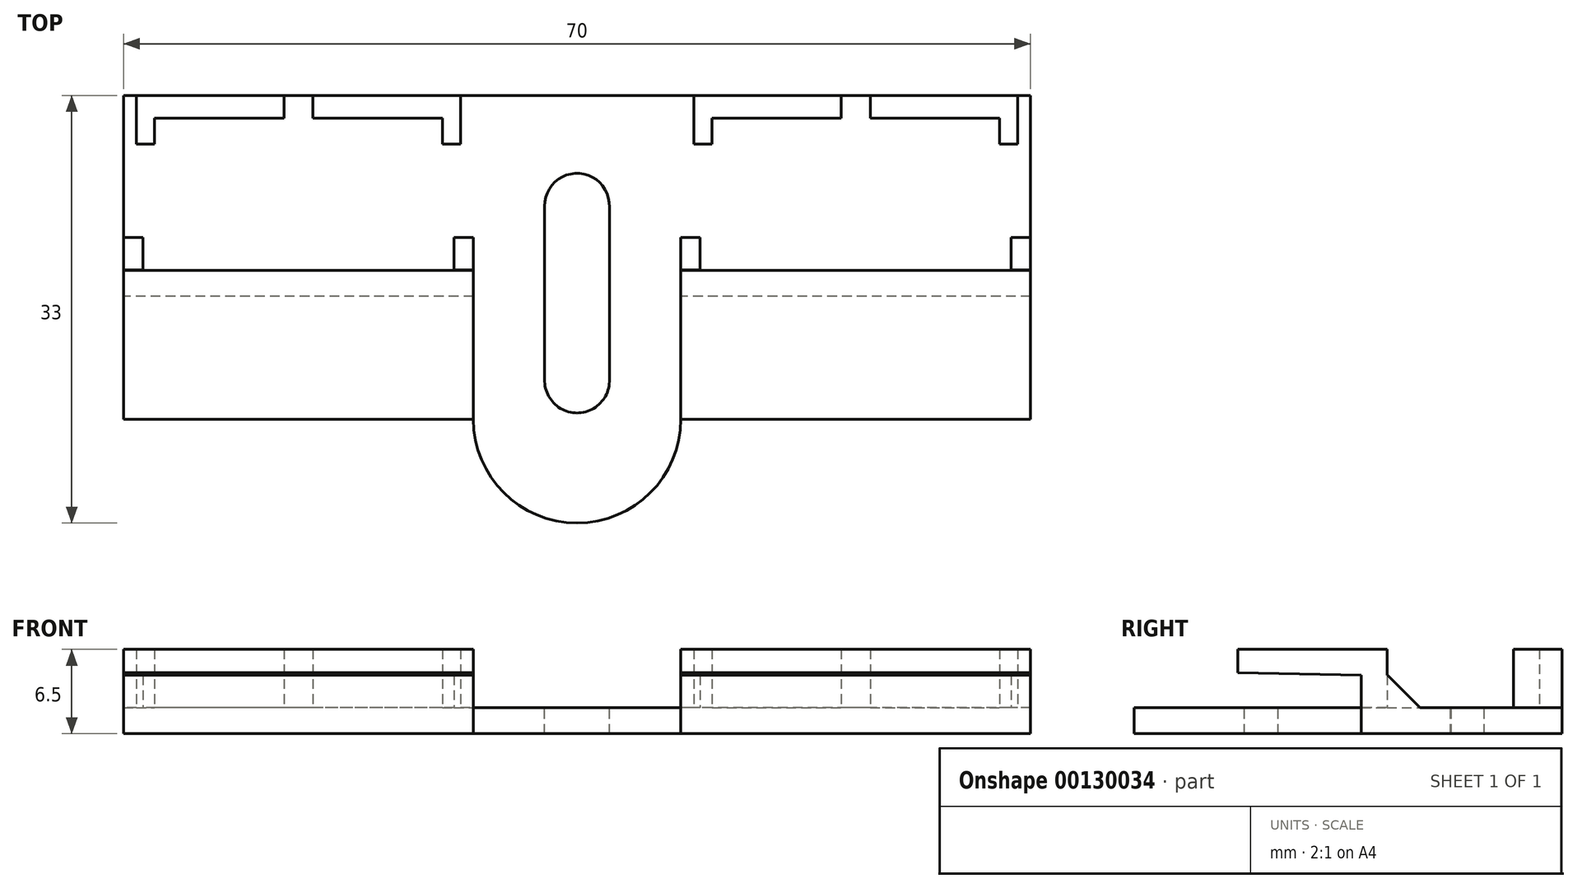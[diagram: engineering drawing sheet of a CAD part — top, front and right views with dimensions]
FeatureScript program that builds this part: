
annotation { "Feature Type Name" : "Feature", "Feature Type Description" : "" }
export const myFeature = defineFeature(function(context is Context, id is Id, definition is map)
    precondition{}
    {
        {
            var Q0;
            Q0=qCreatedBy(makeId("Right.planeOp"),FACE);
            var sketch = newSketch(context, id + "F0", { "sketchPlane" : qUnion([Q0])});
            skLineSegment(sketch, "E0.top", {"start": v(0, 2) * mm, "end": v(-13.5, 2) * mm});
            skLineSegment(sketch, "E0.left", {"start": v(0, 0) * mm, "end": v(0, 2) * mm});
            skLineSegment(sketch, "E1.right", {"start": v(-25, 6.5) * mm, "end": v(-25, 4.7) * mm});
            skLineSegment(sketch, "E2", {"start": v(-25, 4.7) * mm, "end": v(-15.5, 4.5) * mm});
            skLineSegment(sketch, "E3", {"start": v(-13.5, 6.5) * mm, "end": v(-13.5, 2) * mm});
            skLineSegment(sketch, "E4", {"start": v(-25, 6.5) * mm, "end": v(-13.5, 6.5) * mm});
            skLineSegment(sketch, "E5", {"start": v(-15.5, 4.5) * mm, "end": v(-15.5, 0) * mm});
            skLineSegment(sketch, "E6", {"start": v(-15.5, 0) * mm, "end": v(0, 0) * mm});
            skSolve(sketch);
        }
        {
            var Q0;
            Q0=makeQuery(id+"F0.imprint","IMPRINT",FACE,{"disambiguationData":[TD([[makeQuery(id+"F0.imprint","IMPRINT",EDGE,{"derivedFrom":sQuery(id+"F0.wireOp",EDGE,"E0.top")}),1.0]])]});
            extrude(context, id + "F1", {"entities" : qUnion([Q0]), "depth" : 35 * mm, "hasSecondDirection" : true, "secondDirectionOppositeDirection" : true, "secondDirectionDepth" : 35 * mm});
        }
        {
            var Q0;
            Q0=qCreatedBy(makeId("Top.planeOp"),FACE);
            var sketch = newSketch(context, id + "F2", { "sketchPlane" : qUnion([Q0])});
            skLineSegment(sketch, "E7.bottom", {"start": v(-34, 0) * mm, "end": v(-22.63, 0) * mm});
            skLineSegment(sketch, "E7.top", {"start": v(-34, -3.75) * mm, "end": v(-32.6, -3.75) * mm});
            skLineSegment(sketch, "E7.left", {"start": v(-34, 0) * mm, "end": v(-34, -3.75) * mm});
            skLineSegment(sketch, "E7.right", {"start": v(-9, 0) * mm, "end": v(-9, -3.75) * mm});
            skLineSegment(sketch, "E8.top", {"start": v(-10.4, -1.75) * mm, "end": v(-20.38, -1.75) * mm});
            skLineSegment(sketch, "E8.left", {"start": v(-10.4, -3.75) * mm, "end": v(-10.4, -1.75) * mm});
            skLineSegment(sketch, "E8.right", {"start": v(-32.6, -3.75) * mm, "end": v(-32.6, -1.75) * mm});
            skLineSegment(sketch, "E9.trimOffspring", {"start": v(-10.4, -3.75) * mm, "end": v(-9, -3.75) * mm});
            skLineSegment(sketch, "E10.left", {"start": v(-20.38, -1.75) * mm, "end": v(-20.38, 0) * mm});
            skLineSegment(sketch, "E10.right", {"start": v(-22.63, -1.75) * mm, "end": v(-22.63, 0) * mm});
            skLineSegment(sketch, "E11.trimOffspring", {"start": v(-20.38, 0) * mm, "end": v(-9, 0) * mm});
            skLineSegment(sketch, "E12.trimOffspring", {"start": v(-22.63, -1.75) * mm, "end": v(-32.6, -1.75) * mm});
            skLineSegment(sketch, "E13.MirrorCS", {"start": v(9, 0) * mm, "end": v(9, -3.75) * mm});
            skLineSegment(sketch, "E14.MirrorCS", {"start": v(10.4, -3.75) * mm, "end": v(9, -3.75) * mm});
            skLineSegment(sketch, "E15.MirrorCS", {"start": v(10.4, -1.75) * mm, "end": v(20.38, -1.75) * mm});
            skLineSegment(sketch, "E16.MirrorCS", {"start": v(20.38, 0) * mm, "end": v(9, 0) * mm});
            skLineSegment(sketch, "E17.MirrorCS", {"start": v(20.38, -1.75) * mm, "end": v(20.38, 0) * mm});
            skLineSegment(sketch, "E18.MirrorCS", {"start": v(22.63, -1.75) * mm, "end": v(22.63, 0) * mm});
            skLineSegment(sketch, "E19.MirrorCS", {"start": v(22.63, -1.75) * mm, "end": v(32.6, -1.75) * mm});
            skLineSegment(sketch, "E20.MirrorCS", {"start": v(34, 0) * mm, "end": v(22.63, 0) * mm});
            skLineSegment(sketch, "E21.MirrorCS", {"start": v(34, 0) * mm, "end": v(34, -3.75) * mm});
            skLineSegment(sketch, "E22.MirrorCS", {"start": v(34, -3.75) * mm, "end": v(32.6, -3.75) * mm});
            skLineSegment(sketch, "E23.MirrorCS", {"start": v(32.6, -3.75) * mm, "end": v(32.6, -1.75) * mm});
            skLineSegment(sketch, "E24.MirrorCS", {"start": v(10.4, -3.75) * mm, "end": v(10.4, -1.75) * mm});
            skLineSegment(sketch, "E25.bottom", {"start": v(-35, -13.5) * mm, "end": v(-33.5, -13.5) * mm});
            skLineSegment(sketch, "E25.top", {"start": v(-33.5, -10.25) * mm, "end": v(-35, -10.25) * mm});
            skLineSegment(sketch, "E25.left", {"start": v(-33.5, -13.5) * mm, "end": v(-33.5, -10.25) * mm});
            skLineSegment(sketch, "E25.right", {"start": v(-35, -13.5) * mm, "end": v(-35, -10.25) * mm});
            skLineSegment(sketch, "E26.bottom", {"start": v(-8, -13.5) * mm, "end": v(-9.5, -13.5) * mm});
            skLineSegment(sketch, "E26.top", {"start": v(-8, -10.25) * mm, "end": v(-9.5, -10.25) * mm});
            skLineSegment(sketch, "E26.left", {"start": v(-8, -13.5) * mm, "end": v(-8, -10.25) * mm});
            skLineSegment(sketch, "E26.right", {"start": v(-9.5, -13.5) * mm, "end": v(-9.5, -10.25) * mm});
            skLineSegment(sketch, "E27.MirrorCS", {"start": v(8, -13.5) * mm, "end": v(8, -10.25) * mm});
            skLineSegment(sketch, "E28.MirrorCS", {"start": v(8, -13.5) * mm, "end": v(9.5, -13.5) * mm});
            skLineSegment(sketch, "E29.MirrorCS", {"start": v(8, -10.25) * mm, "end": v(9.5, -10.25) * mm});
            skLineSegment(sketch, "E30.MirrorCS", {"start": v(9.5, -13.5) * mm, "end": v(9.5, -10.25) * mm});
            skLineSegment(sketch, "E31.MirrorCS", {"start": v(33.5, -13.5) * mm, "end": v(33.5, -10.25) * mm});
            skLineSegment(sketch, "E32.MirrorCS", {"start": v(35, -13.5) * mm, "end": v(35, -10.25) * mm});
            skLineSegment(sketch, "E33.MirrorCS", {"start": v(33.5, -10.25) * mm, "end": v(35, -10.25) * mm});
            skLineSegment(sketch, "E34.MirrorCS", {"start": v(35, -13.5) * mm, "end": v(33.5, -13.5) * mm});
            skPoint(sketch, "E35", {"position": v(21.5, -7.63) * mm});
            skPoint(sketch, "E36", {"position": v(-21.5, -7.63) * mm});
            skSolve(sketch);
        }
        {
            var Q0;
            Q0=makeQuery(id+"F2.imprint","IMPRINT",FACE,{"disambiguationData":[TD([[makeQuery(id+"F2.imprint","IMPRINT",EDGE,{"derivedFrom":sQuery(id+"F2.wireOp",EDGE,"E7.bottom")}),-1.0]])]});
            var Q1;
            Q1=makeQuery(id+"F2.imprint","IMPRINT",FACE,{"disambiguationData":[TD([[makeQuery(id+"F2.imprint","IMPRINT",EDGE,{"derivedFrom":sQuery(id+"F2.wireOp",EDGE,"E7.right")}),-1.0]])]});
            var Q2;
            Q2=makeQuery(id+"F2.imprint","IMPRINT",FACE,{"disambiguationData":[TD([[makeQuery(id+"F2.imprint","IMPRINT",EDGE,{"derivedFrom":sQuery(id+"F2.wireOp",EDGE,"E13.MirrorCS")}),1.0]])]});
            var Q3;
            Q3=makeQuery(id+"F2.imprint","IMPRINT",FACE,{"disambiguationData":[TD([[makeQuery(id+"F2.imprint","IMPRINT",EDGE,{"derivedFrom":sQuery(id+"F2.wireOp",EDGE,"E18.MirrorCS")}),-1.0]])]});
            extrude(context, id + "F3", {"entities" : qUnion([Q0, Q1, Q2, Q3]), "operationType" : NewBodyOperationType.ADD, "depth" : 6.5 * mm});
        }
        {
            var Q0;
            Q0=makeQuery(id+"F2.imprint","IMPRINT",FACE,{"disambiguationData":[TD([[makeQuery(id+"F2.imprint","IMPRINT",EDGE,{"derivedFrom":sQuery(id+"F2.wireOp",EDGE,"E27.MirrorCS")}),-1.0]])]});
            var Q1;
            Q1=makeQuery(id+"F2.imprint","IMPRINT",FACE,{"disambiguationData":[TD([[makeQuery(id+"F2.imprint","IMPRINT",EDGE,{"derivedFrom":sQuery(id+"F2.wireOp",EDGE,"E25.bottom")}),1.0]])]});
            var Q2;
            Q2=makeQuery(id+"F2.imprint","IMPRINT",FACE,{"disambiguationData":[TD([[makeQuery(id+"F2.imprint","IMPRINT",EDGE,{"derivedFrom":sQuery(id+"F2.wireOp",EDGE,"E26.bottom")}),-1.0]])]});
            var Q3;
            Q3=makeQuery(id+"F2.imprint","IMPRINT",FACE,{"disambiguationData":[TD([[makeQuery(id+"F2.imprint","IMPRINT",EDGE,{"derivedFrom":sQuery(id+"F2.wireOp",EDGE,"E31.MirrorCS")}),-1.0]])]});
            extrude(context, id + "F4", {"entities" : qUnion([Q0, Q1, Q2, Q3]), "operationType" : NewBodyOperationType.ADD, "depth" : 4.5 * mm, "hasSecondDirection" : true, "secondDirectionOppositeDirection" : false, "secondDirectionDepth" : 2 * mm});
        }
        {
            var Q0;
            Q0=qCreatedBy(makeId("Front.planeOp"),FACE);
            var sketch = newSketch(context, id + "F5", { "sketchPlane" : qUnion([Q0])});
            skLineSegment(sketch, "E37.bottom", {"start": v(8, 2) * mm, "end": v(-8, 2) * mm});
            skLineSegment(sketch, "E37.top", {"start": v(8, 6.5) * mm, "end": v(-8, 6.5) * mm});
            skLineSegment(sketch, "E37.left", {"start": v(8, 2) * mm, "end": v(8, 6.5) * mm});
            skLineSegment(sketch, "E37.right", {"start": v(-8, 2) * mm, "end": v(-8, 6.5) * mm});
            skLineSegment(sketch, "E38.top", {"start": v(8, 0) * mm, "end": v(-8, 0) * mm});
            skLineSegment(sketch, "E38.left", {"start": v(8, 2) * mm, "end": v(8, 0) * mm});
            skLineSegment(sketch, "E38.right", {"start": v(-8, 2) * mm, "end": v(-8, 0) * mm});
            skSolve(sketch);
        }
        {
            var Q0;
            Q0=makeQuery(id+"F5.imprint","IMPRINT",FACE,{"disambiguationData":[TD([[makeQuery(id+"F5.imprint","IMPRINT",EDGE,{"derivedFrom":sQuery(id+"F5.wireOp",EDGE,"E37.top")}),1.0]])]});
            extrude(context, id + "F6", {"entities" : qUnion([Q0]), "operationType" : NewBodyOperationType.REMOVE, "depth" : 25 * mm});
        }
        {
            var Q0;
            Q0=makeQuery(id+"F4.opExtrude","CAP_EDGE",EDGE,{"disambiguationData":[OSD([sQuery(id+"F2.wireOp",EDGE,"E33.MirrorCS")])],"isStart":false});
            var Q1;
            Q1=makeQuery(id+"F4.opExtrude","CAP_EDGE",EDGE,{"disambiguationData":[OSD([sQuery(id+"F2.wireOp",EDGE,"E29.MirrorCS")])],"isStart":false});
            var Q2;
            Q2=makeQuery(id+"F4.opExtrude","CAP_EDGE",EDGE,{"disambiguationData":[OSD([sQuery(id+"F2.wireOp",EDGE,"E26.top")])],"isStart":false});
            var Q3;
            Q3=makeQuery(id+"F4.opExtrude","CAP_EDGE",EDGE,{"disambiguationData":[OSD([sQuery(id+"F2.wireOp",EDGE,"E25.top")])],"isStart":false});
            chamfer(context, id + "F7", {"entities" : qUnion([Q0, Q1, Q2, Q3]), "width" : 3.2 * mm, "tangentPropagation" : true});
        }
        {
            var Q0;
            {var subQ2=sQuery(id+"F0.wireOp",EDGE,"E0.top");Q0=makeQuery(id+"F6.boolean.opBoolean","SPLIT",FACE,{"disambiguationData":[TD([makeQuery(id+"F3.opExtrude","SWEPT_FACE",FACE,{"disambiguationData":[OSD([sQuery(id+"F2.wireOp",EDGE,"E13.MirrorCS")])]})])],"derivedFrom":makeQuery(id+"F1.opExtrude","SWEPT_FACE",FACE,{"disambiguationData":[OSD([subQ2])]})});}
            var sketch = newSketch(context, id + "F8", { "sketchPlane" : qUnion([Q0])});
            skPoint(sketch, "E39", {"position": v(21.5, -7.63) * mm});
            skPoint(sketch, "E40", {"position": v(-21.5, -7.63) * mm});
            skSolve(sketch);
        }
        {
            var Q0;
            Q0=makeQuery(id+"F5.imprint","IMPRINT",FACE,{"disambiguationData":[TD([[makeQuery(id+"F5.imprint","IMPRINT",EDGE,{"derivedFrom":sQuery(id+"F5.wireOp",EDGE,"E37.bottom")}),1.0]])]});
            extrude(context, id + "F9", {"entities" : qUnion([Q0]), "operationType" : NewBodyOperationType.ADD, "depth" : 33 * mm});
        }
        {
            var Q0;
            {var subQ0=sQuery(id+"F5.wireOp",EDGE,"E37.bottom");Q0=makeQuery(id+"F9.boolean.opBoolean","MERGE",FACE,{"derivedFrom":[makeQuery(id+"F6.boolean.opBoolean","COPY",FACE,{"derivedFrom":makeQuery(id+"F6.opExtrude","SWEPT_FACE",FACE,{"disambiguationData":[OSD([subQ0])]})}),makeQuery(id+"F9.opExtrude","SWEPT_FACE",FACE,{"disambiguationData":[OSD([subQ0])]})]});}
            var sketch = newSketch(context, id + "F10", { "sketchPlane" : qUnion([Q0])});
            skPoint(sketch, "E41", {"position": v(0, -22) * mm});
            skPoint(sketch, "E41.positionSnap0", {"position": v(0, -33) * mm});
            skPoint(sketch, "E42", {"position": v(0, -8.5) * mm});
            skArc(sketch, "E43", {"start": v(2.5, -8.6) * mm, "mid": v(0.02, -6) * mm, "end": v(-2.5, -8.54) * mm});
            skArc(sketch, "E44", {"start": v(-2.5, -21.9) * mm, "mid": v(0, -24.5) * mm, "end": v(2.5, -21.9) * mm});
            skLineSegment(sketch, "E45.top", {"start": v(-2.5, -21.9) * mm, "end": v(-2.5, -21.9) * mm});
            skLineSegment(sketch, "E45.left", {"start": v(-2.5, -8.54) * mm, "end": v(-2.5, -21.9) * mm});
            skLineSegment(sketch, "E45.right", {"start": v(2.5, -8.54) * mm, "end": v(2.5, -21.9) * mm});
            skSolve(sketch);
        }
        {
            var Q0;
            Q0=makeQuery(id+"F9.opExtrude","CAP_EDGE",EDGE,{"disambiguationData":[OSD([sQuery(id+"F5.wireOp",EDGE,"E38.left")])],"isStart":false});
            var Q1;
            Q1=makeQuery(id+"F9.opExtrude","CAP_EDGE",EDGE,{"disambiguationData":[OSD([sQuery(id+"F5.wireOp",EDGE,"E38.right")])],"isStart":false});
            fillet(context, id + "F11", {"entities" : qUnion([Q0, Q1]), "radius" : 8 * mm, "tangentPropagation" : true, "allowEdgeOverflow" : false});
        }
        {
            var Q0;
            {var subQ1=sQuery(id+"F10.wireOp",EDGE,"E44");Q0=makeQuery(id+"F10.imprint","IMPRINT",FACE,{"disambiguationData":[TD([[makeQuery(id+"F10.imprint","IMPRINT",EDGE,{"derivedFrom":subQ1}),1.0]])]});}
            var Q1;
            {var subQ0=sQuery(id+"F10.wireOp",EDGE,"E43");Q1=makeQuery(id+"F10.imprint","IMPRINT",FACE,{"disambiguationData":[TD([[makeQuery(id+"F10.imprint","IMPRINT",EDGE,{"derivedFrom":subQ0}),1.0]])]});}
            extrude(context, id + "F12", {"entities" : qUnion([Q0, Q1]), "operationType" : NewBodyOperationType.REMOVE, "oppositeDirection" : true, "depth" : 25 * mm});
        }
    });
